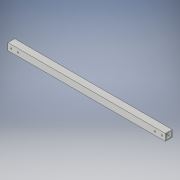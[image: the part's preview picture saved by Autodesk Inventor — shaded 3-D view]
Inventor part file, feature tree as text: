
AUTODESK INVENTOR PART (.ipt)
format: ipt  version: 2018 (Build 220112000, 112)  size: 121,344 bytes
history: native  units: in
note: dims shown in document units (in); Inventor stores cm internally (conversion verified against a paired STEP export)
features: extrude x2, sketch x2
ambient origin geometry x8: Origin, YZ Plane, XZ Plane, XY Plane, X Axis, Y Axis, Z Axis, Center Point
bodies: Solid1 (feature_tree)
feature tree (4):
  extrude  "Extrusion1"  Depth=1.0in
  extrude  "Extrusion3"  Depth=23.0in TaperAngle=0.0deg
  sketch  "Sketch1"  dims[d0=1.0in d1=1.0in]
  sketch  "Sketch3"  dims[d2=0.125in d3=23.0in d4=0.0in d7=0.5in d8=1.0in d9=0.5in d10=1.0in d11=0.2031in d12=0.2031in d13=0.2031in d14=0.2031in d15=23.0in d16=0.0in]
